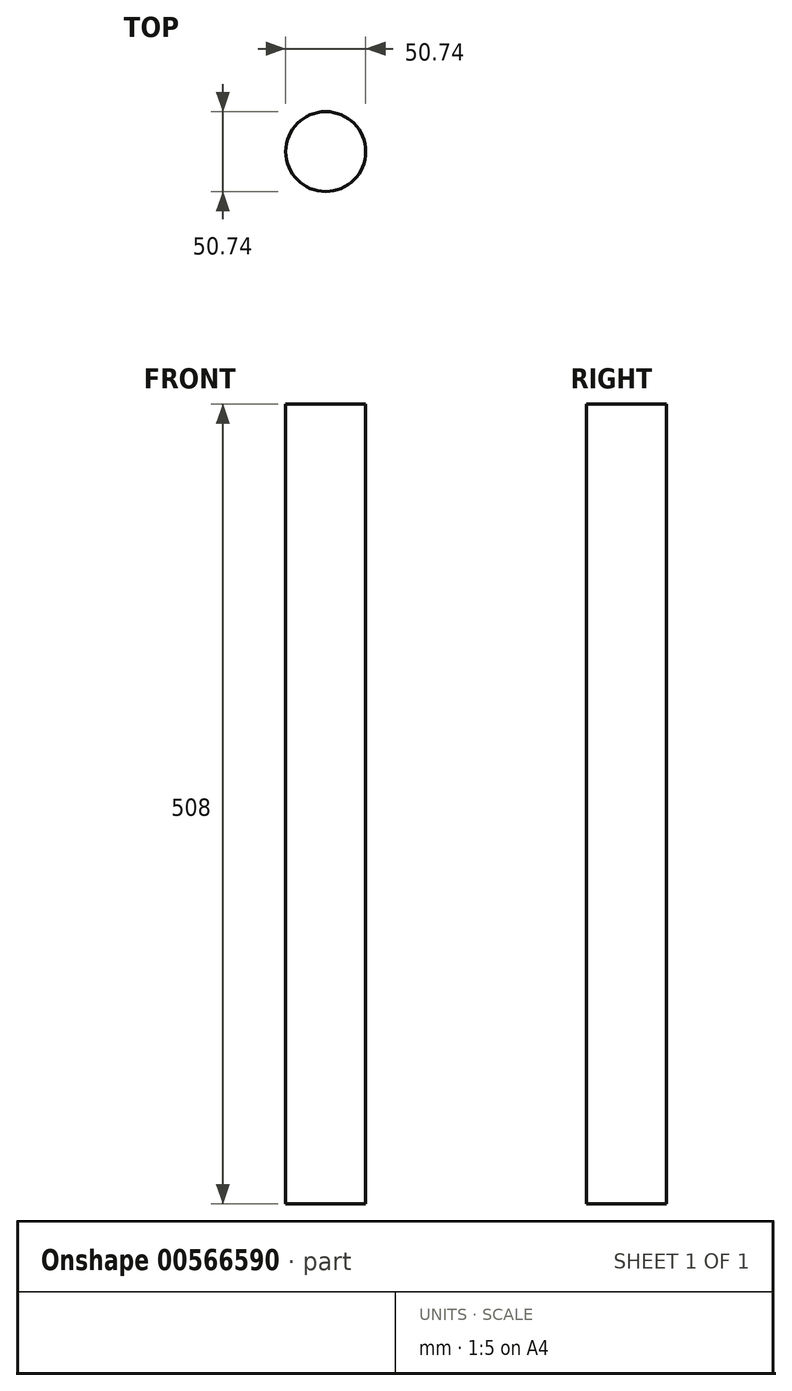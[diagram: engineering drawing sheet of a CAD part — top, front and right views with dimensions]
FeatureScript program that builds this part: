
annotation { "Feature Type Name" : "Feature", "Feature Type Description" : "" }
export const myFeature = defineFeature(function(context is Context, id is Id, definition is map)
    precondition{}
    {
        {
            var Q0;
            Q0=qCreatedBy(makeId("Top.planeOp"),FACE);
            var sketch = newSketch(context, id + "F0", { "sketchPlane" : qUnion([Q0])});
            skCircle(sketch, "E0", {"center": v(0, 0) * mm, "radius": 25.37 * mm});
            skSolve(sketch);
        }
        {
            var Q0;
            Q0=makeQuery(id+"F0.imprint","IMPRINT",FACE,{"disambiguationData":[TD([[makeQuery(id+"F0.imprint","IMPRINT",EDGE,{"derivedFrom":sQuery(id+"F0.wireOp",EDGE,"E0")}),1.0]])]});
            extrude(context, id + "F1", {"entities" : qUnion([Q0]), "depth" : 508 * mm, "offsetDistance" : 25.4 * mm});
        }
    });
